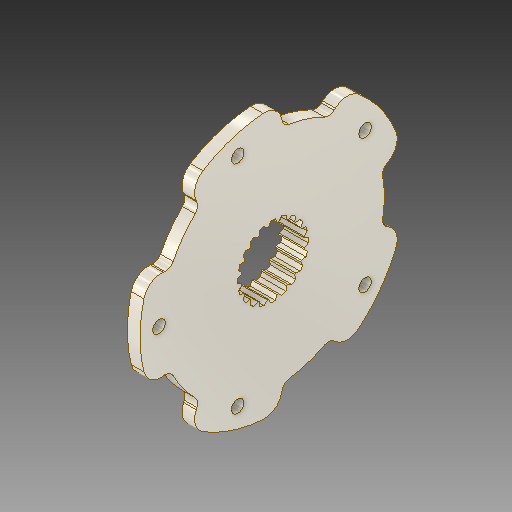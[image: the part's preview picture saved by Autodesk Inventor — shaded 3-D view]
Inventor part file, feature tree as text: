
AUTODESK INVENTOR PART (.ipt)
format: ipt  version: 2019 (Build 230136000, 136)  size: 338,944 bytes
history: native  units: mm
features: extrude x4, sketch x3, pattern_circular x1
ambient origin geometry x8: Origin, YZ Plane, XZ Plane, XY Plane, X Axis, Y Axis, Z Axis, Center Point
bodies: Solid1 (feature_tree)
feature tree (8):
  extrude  "Extrusion1"  Depth=5.0mm
  extrude  "Extrusion2"  Depth=5.0mm
  extrude  "Extrusion3"  Depth=10.0mm TaperAngle=0.0deg
  pattern_circular  "Circular Pattern1"  Count=5 Angle=360.0deg
  extrude  "Extrusion4"  Depth=10.0mm TaperAngle=0.0deg
  sketch  "Sketch1"  dims[d102=5.0mm d103=0.0mm d104=65.0mm]
  sketch  "Sketch2"  dims[d105=5.0mm d106=0.0mm d107=5.0mm]
  sketch  "Sketch3"  dims[d108=45.0mm d109=10.0mm d110=0.0mm d111=50.0mm d112=360.0deg d114=10.0mm d115=0.0mm d117=50.0mm d118=52.5mm d119=7.0mm d120=3.25mm d121=360.0deg d122=44.0mm d123=12.5mm d124=19.5mm d126=200.0mm d127=25.0mm d128=1.8mm d129=14.0mm d130=20.245819mm d131=360.0deg]
